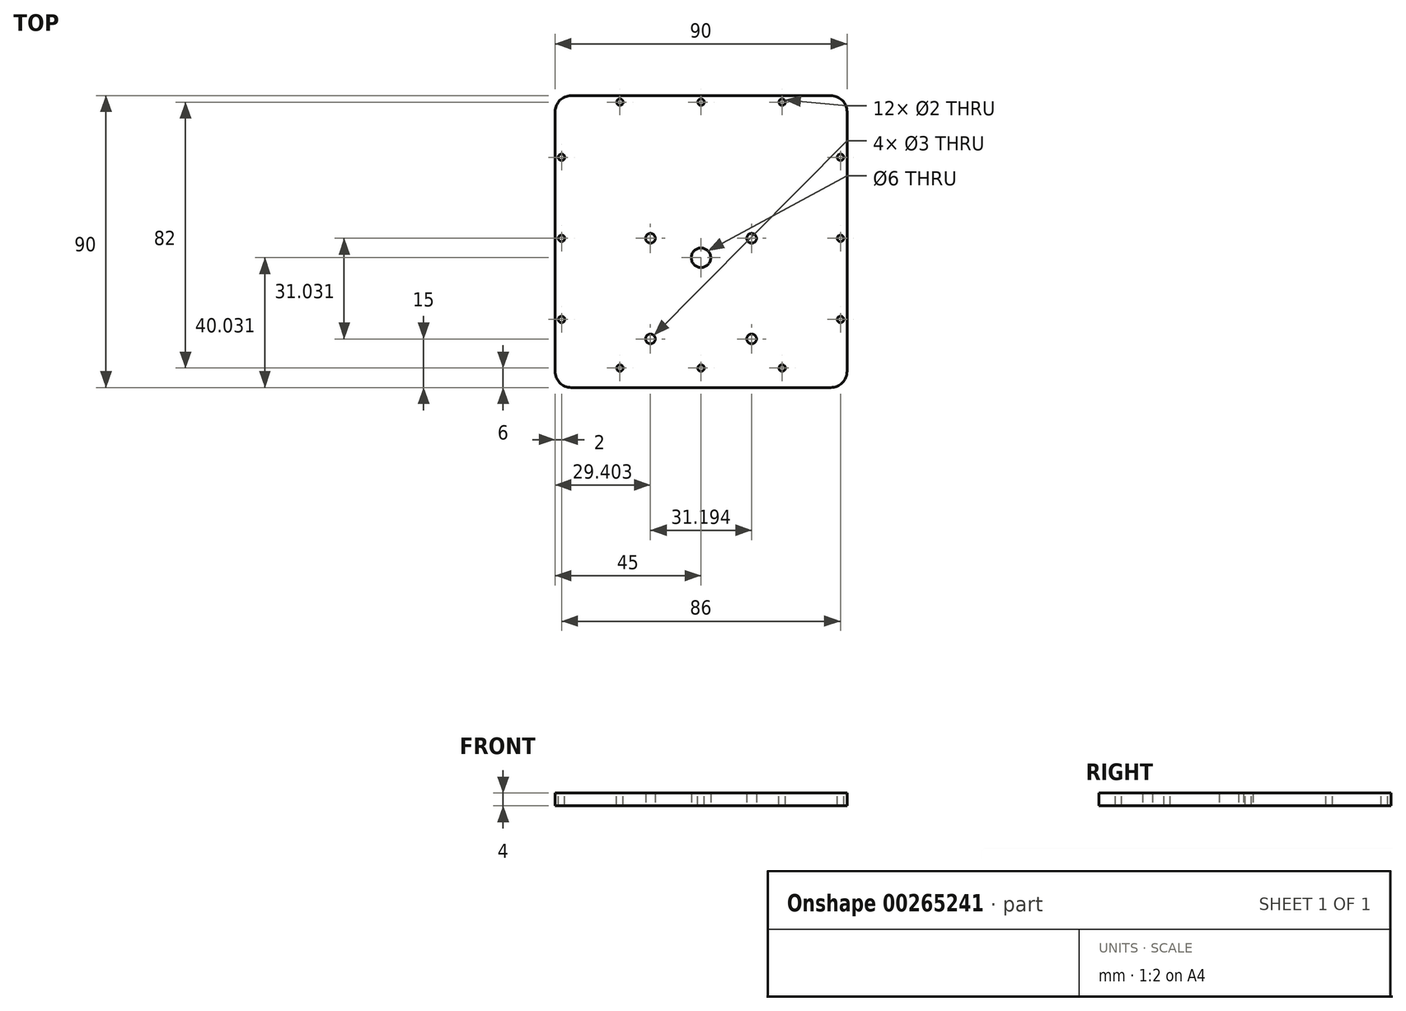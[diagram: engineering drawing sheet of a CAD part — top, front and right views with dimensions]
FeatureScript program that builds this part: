
annotation { "Feature Type Name" : "Feature", "Feature Type Description" : "" }
export const myFeature = defineFeature(function(context is Context, id is Id, definition is map)
    precondition{}
    {
        {
            var Q0;
            Q0=qCreatedBy(makeId("Top.planeOp"),FACE);
            var sketch = newSketch(context, id + "F0", { "sketchPlane" : qUnion([Q0])});
            skLineSegment(sketch, "E0.bottom", {"start": v(45, -45) * mm, "end": v(-45, -45) * mm});
            skLineSegment(sketch, "E0.top", {"start": v(45, 45) * mm, "end": v(-45, 45) * mm});
            skLineSegment(sketch, "E0.left", {"start": v(45, -45) * mm, "end": v(45, 45) * mm});
            skLineSegment(sketch, "E0.right", {"start": v(-45, -45) * mm, "end": v(-45, 45) * mm});
            skPoint(sketch, "E0.middle", {"position": v(0, 0) * mm});
            skPoint(sketch, "E1", {"position": v(-15.6, 1.03) * mm});
            skPoint(sketch, "E2", {"position": v(15.6, 1.03) * mm});
            skPoint(sketch, "E3", {"position": v(15.6, -30) * mm});
            skPoint(sketch, "E4", {"position": v(-15.6, -30) * mm});
            skPoint(sketch, "E5", {"position": v(0, -4.97) * mm});
            skCircle(sketch, "E6", {"center": v(-15.6, 1.03) * mm, "radius": 1.5 * mm});
            skCircle(sketch, "E7", {"center": v(15.6, 1.03) * mm, "radius": 1.5 * mm});
            skCircle(sketch, "E8", {"center": v(15.6, -30) * mm, "radius": 1.5 * mm});
            skCircle(sketch, "E9", {"center": v(-15.6, -30) * mm, "radius": 1.5 * mm});
            skCircle(sketch, "E10", {"center": v(0, -4.97) * mm, "radius": 3 * mm});
            skSolve(sketch);
        }
        {
            var Q0;
            Q0 = qSketchRegion(id + "F0", true);
            extrude(context, id + "F1", {"entities" : qUnion([Q0]), "depth" : 4 * mm});
        }
        {
            var Q0;
            Q0=makeQuery(id+"F1.opExtrude","SWEPT_EDGE",EDGE,{"disambiguationData":[OSD([sQuery(id+"F0.wireOp",EDGE,"E0.bottom"),sQuery(id+"F0.wireOp",EDGE,"E0.right")])]});
            var Q1;
            Q1=makeQuery(id+"F1.opExtrude","SWEPT_EDGE",EDGE,{"disambiguationData":[OSD([sQuery(id+"F0.wireOp",EDGE,"E0.bottom"),sQuery(id+"F0.wireOp",EDGE,"E0.left")])]});
            var Q2;
            Q2=makeQuery(id+"F1.opExtrude","SWEPT_EDGE",EDGE,{"disambiguationData":[OSD([sQuery(id+"F0.wireOp",EDGE,"E0.top"),sQuery(id+"F0.wireOp",EDGE,"E0.left")])]});
            var Q3;
            Q3=makeQuery(id+"F1.opExtrude","SWEPT_EDGE",EDGE,{"disambiguationData":[OSD([sQuery(id+"F0.wireOp",EDGE,"E0.top"),sQuery(id+"F0.wireOp",EDGE,"E0.right")])]});
            fillet(context, id + "F2", {"entities" : qUnion([Q0, Q1, Q2, Q3]), "radius" : 5 * mm, "tangentPropagation" : true, "allowEdgeOverflow" : false});
        }
        {
            var Q0;
            Q0=makeQuery(id+"F1.opExtrude","CAP_FACE",FACE,{"disambiguationData":[OSD([sQuery(id+"F0.wireOp",EDGE,"E0.bottom"),sQuery(id+"F0.wireOp",EDGE,"E0.top"),sQuery(id+"F0.wireOp",EDGE,"E0.left"),sQuery(id+"F0.wireOp",EDGE,"E0.right"),sQuery(id+"F0.wireOp",EDGE,"E6"),sQuery(id+"F0.wireOp",EDGE,"E7"),sQuery(id+"F0.wireOp",EDGE,"E8"),sQuery(id+"F0.wireOp",EDGE,"E9"),sQuery(id+"F0.wireOp",EDGE,"E10")])],"isStart":false});
            var sketch = newSketch(context, id + "F3", { "sketchPlane" : qUnion([Q0])});
            skCircle(sketch, "E11", {"center": v(0, 43) * mm, "radius": 2 * mm});
            skCircle(sketch, "E12", {"center": v(43, 1) * mm, "radius": 2 * mm});
            skCircle(sketch, "E13", {"center": v(-43, 1) * mm, "radius": 2 * mm});
            skCircle(sketch, "E14", {"center": v(25, 43) * mm, "radius": 2 * mm});
            skCircle(sketch, "E15", {"center": v(-25, 43) * mm, "radius": 2 * mm});
            skCircle(sketch, "E16", {"center": v(43, -24) * mm, "radius": 2 * mm});
            skCircle(sketch, "E17", {"center": v(-43, 26) * mm, "radius": 2 * mm});
            skCircle(sketch, "E18", {"center": v(43, 26) * mm, "radius": 2 * mm});
            skCircle(sketch, "E19", {"center": v(0, -39) * mm, "radius": 2 * mm});
            skCircle(sketch, "E20", {"center": v(25, -39) * mm, "radius": 2 * mm});
            skCircle(sketch, "E21", {"center": v(-25, -39) * mm, "radius": 2 * mm});
            skCircle(sketch, "E22", {"center": v(-43, -24) * mm, "radius": 2 * mm});
            skSolve(sketch);
        }
        {
            var Q0;
            Q0=sQuery(id+"F3.wireOp",VERTEX,"E15.center");
            var Q1;
            Q1=sQuery(id+"F3.wireOp",VERTEX,"E17.center");
            var Q2;
            Q2=sQuery(id+"F3.wireOp",VERTEX,"E13.center");
            var Q3;
            Q3=sQuery(id+"F3.wireOp",VERTEX,"E22.center");
            var Q4;
            Q4=sQuery(id+"F3.wireOp",VERTEX,"E21.center");
            var Q5;
            Q5=sQuery(id+"F3.wireOp",VERTEX,"E19.center");
            var Q6;
            Q6=sQuery(id+"F3.wireOp",VERTEX,"E20.center");
            var Q7;
            Q7=sQuery(id+"F3.wireOp",VERTEX,"E16.center");
            var Q8;
            Q8=sQuery(id+"F3.wireOp",VERTEX,"E12.center");
            var Q9;
            Q9=sQuery(id+"F3.wireOp",VERTEX,"E18.center");
            var Q10;
            Q10=sQuery(id+"F3.wireOp",VERTEX,"E14.center");
            var Q11;
            Q11=sQuery(id+"F3.wireOp",VERTEX,"E11.center");
            var Q12;
            Q12=makeQuery(id+"F1.opExtrude","SWEPT_BODY",BODY,{"disambiguationData":[OSD([sQuery(id+"F0.wireOp",EDGE,"E0.bottom"),sQuery(id+"F0.wireOp",EDGE,"E0.top"),sQuery(id+"F0.wireOp",EDGE,"E0.left"),sQuery(id+"F0.wireOp",EDGE,"E0.right"),sQuery(id+"F0.wireOp",EDGE,"E6"),sQuery(id+"F0.wireOp",EDGE,"E7"),sQuery(id+"F0.wireOp",EDGE,"E8"),sQuery(id+"F0.wireOp",EDGE,"E9"),sQuery(id+"F0.wireOp",EDGE,"E10")])]});
            hole(context, id + "F4", {"style" : HoleStyle.SIMPLE, "endStyle" : HoleEndStyle.BLIND, "holeDiameter" : 2 * mm, "holeDepth" : 6 * mm, "tappedDepth" : 12 * mm, "tapClearance" : 3, "locations" : qUnion([Q0, Q1, Q2, Q3, Q4, Q5, Q6, Q7, Q8, Q9, Q10, Q11]), "scope" : qUnion([Q12])});
        }
    });
